# Revit family: Door_Purso_LK100eco_Sliding-door
name_source: partatom
category: Doors
revit_build: Autodesk Revit 2018 (Build: 20170223_1515(x64)
units: mm (PartAtom-declared; Revit-internal decimal feet)

## family parameters
Always vertical = Yes
Cut with Voids When Loaded = No
Host = Wall
OmniClass Number = 23.30.10.00
OmniClass Title = Doors
Room Calculation Point = No
Shared = No

## types (1)
- Door_Purso_LK100eco_Sliding-door
    Analytic Construction = <None>
    Assembly Code = B2030
    Description = "Thermally highly insulated Lift and Slide Door system"
    Edition number = 1
    Frame Material = Default
    Handle Material = Aluminium - Purso - Aluminium
    Height = 2100 mm
    Keynote = 08 11 00
    Leaf Material = Default
    Manufacturer = "Purso"
    Model = LK100eco sliding door
    Product Guid = b6f2ea23-11a1-4f19-a303-76ee2267e814
    Product data url = https://www.bimobject.com
    URL = https://purso.fi
    Wall Closure = By host
    Width = 2300 mm

## geometry (parser evidence)
native form markers: Sweep x5
no freeform markers — native parametric forms only
